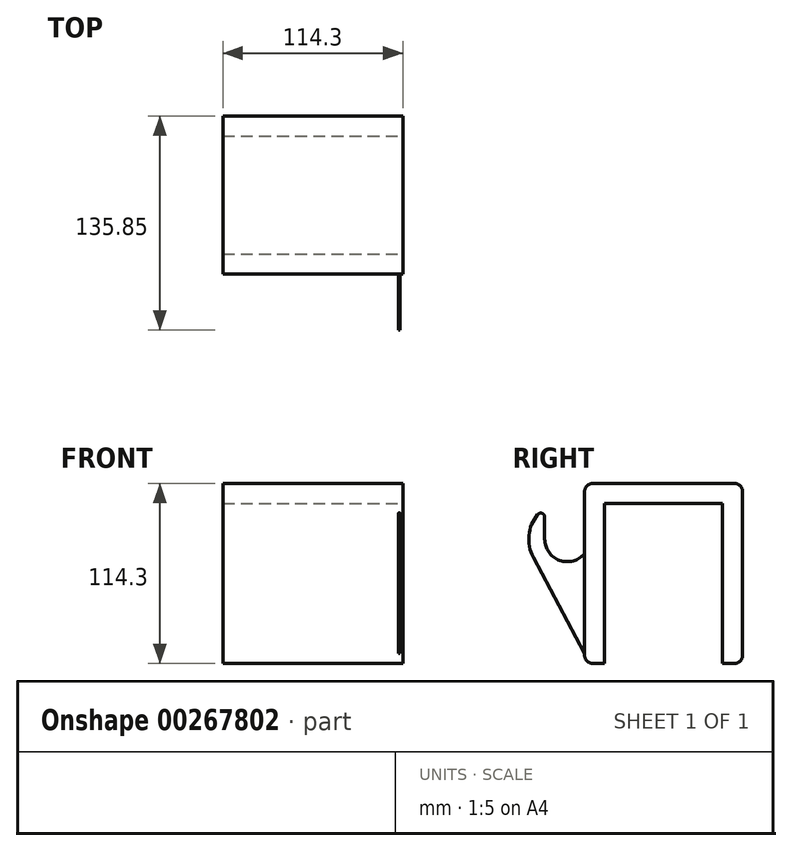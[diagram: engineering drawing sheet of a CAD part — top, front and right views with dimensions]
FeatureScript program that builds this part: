
annotation { "Feature Type Name" : "Feature", "Feature Type Description" : "" }
export const myFeature = defineFeature(function(context is Context, id is Id, definition is map)
    precondition{}
    {
        {
            var Q0;
            Q0=qCreatedBy(makeId("Top.planeOp"),FACE);
            var sketch = newSketch(context, id + "F0", { "sketchPlane" : qUnion([Q0])});
            skLineSegment(sketch, "E0.bottom", {"start": v(-114.3, 74.93) * mm, "end": v(0, 74.93) * mm});
            skLineSegment(sketch, "E0.top", {"start": v(-114.3, 0) * mm, "end": v(0, 0) * mm});
            skLineSegment(sketch, "E0.left", {"start": v(-114.3, 74.93) * mm, "end": v(-114.3, 0) * mm});
            skLineSegment(sketch, "E0.right", {"start": v(0, 74.93) * mm, "end": v(0, 0) * mm});
            skLineSegment(sketch, "E1", {"start": v(-114.3, 0) * mm, "end": v(-114.3, -12.7) * mm});
            skLineSegment(sketch, "E2", {"start": v(-114.3, -12.7) * mm, "end": v(0, -12.7) * mm});
            skLineSegment(sketch, "E3", {"start": v(0, -12.7) * mm, "end": v(0, 0) * mm});
            skLineSegment(sketch, "E4", {"start": v(-114.3, 74.93) * mm, "end": v(-114.3, 87.63) * mm});
            skLineSegment(sketch, "E5", {"start": v(-114.3, 87.63) * mm, "end": v(0, 87.63) * mm});
            skLineSegment(sketch, "E6", {"start": v(0, 87.63) * mm, "end": v(0, 74.93) * mm});
            skLineSegment(sketch, "E7", {"start": v(-101.6, 87.63) * mm, "end": v(-101.6, 74.93) * mm});
            skLineSegment(sketch, "E8", {"start": v(-12.7, 87.63) * mm, "end": v(-12.7, 74.93) * mm});
            skLineSegment(sketch, "E9", {"start": v(-12.7, 0) * mm, "end": v(-12.7, -12.7) * mm});
            skLineSegment(sketch, "E10", {"start": v(-101.6, 0) * mm, "end": v(-101.6, -12.7) * mm});
            skLineSegment(sketch, "E11", {"start": v(-101.6, 74.93) * mm, "end": v(-101.6, 0) * mm, "construction": true});
            skLineSegment(sketch, "E12", {"start": v(-12.7, 74.93) * mm, "end": v(-12.7, 0) * mm, "construction": true});
            skSolve(sketch);
        }
        {
            var Q0;
            {var subQ0=sQuery(id+"F0.wireOp",EDGE,"E0.left");Q0=makeQuery(id+"F0.imprint","IMPRINT",FACE,{"disambiguationData":[TD([[makeQuery(id+"F0.imprint","IMPRINT",EDGE,{"derivedFrom":subQ0}),1.0]])]});}
            extrude(context, id + "F1", {"entities" : qUnion([Q0]), "oppositeDirection" : true, "depth" : 12.7 * mm});
        }
        {
            var Q0;
            {var subQ0=sQuery(id+"F0.wireOp",EDGE,"E4");Q0=makeQuery(id+"F0.imprint","IMPRINT",FACE,{"disambiguationData":[TD([[makeQuery(id+"F0.imprint","IMPRINT",EDGE,{"derivedFrom":subQ0}),-1.0]])]});}
            var Q1;
            {var subQ0=sQuery(id+"F0.wireOp",EDGE,"E7");Q1=makeQuery(id+"F0.imprint","IMPRINT",FACE,{"disambiguationData":[TD([[makeQuery(id+"F0.imprint","IMPRINT",EDGE,{"derivedFrom":subQ0}),1.0]])]});}
            var Q2;
            {var subQ0=sQuery(id+"F0.wireOp",EDGE,"E6");Q2=makeQuery(id+"F0.imprint","IMPRINT",FACE,{"disambiguationData":[TD([[makeQuery(id+"F0.imprint","IMPRINT",EDGE,{"derivedFrom":subQ0}),-1.0]])]});}
            var Q3;
            {var subQ0=sQuery(id+"F0.wireOp",EDGE,"E3");Q3=makeQuery(id+"F0.imprint","IMPRINT",FACE,{"disambiguationData":[TD([[makeQuery(id+"F0.imprint","IMPRINT",EDGE,{"derivedFrom":subQ0}),1.0]])]});}
            var Q4;
            {var subQ0=sQuery(id+"F0.wireOp",EDGE,"E9");Q4=makeQuery(id+"F0.imprint","IMPRINT",FACE,{"disambiguationData":[TD([[makeQuery(id+"F0.imprint","IMPRINT",EDGE,{"derivedFrom":subQ0}),-1.0]])]});}
            var Q5;
            {var subQ0=sQuery(id+"F0.wireOp",EDGE,"E1");Q5=makeQuery(id+"F0.imprint","IMPRINT",FACE,{"disambiguationData":[TD([[makeQuery(id+"F0.imprint","IMPRINT",EDGE,{"derivedFrom":subQ0}),1.0]])]});}
            extrude(context, id + "F2", {"entities" : qUnion([Q0, Q1, Q2, Q3, Q4, Q5]), "operationType" : NewBodyOperationType.ADD, "oppositeDirection" : true, "depth" : 114.3 * mm});
        }
        {
            var Q0;
            Q0=qCreatedBy(makeId("Right.planeOp"),FACE);
            var sketch = newSketch(context, id + "F3", { "sketchPlane" : qUnion([Q0])});
            skLineSegment(sketch, "E13", {"start": v(0, 0) * mm, "end": v(-12.7, 0) * mm, "construction": true});
            skLineSegment(sketch, "E14", {"start": v(-12.7, 0) * mm, "end": v(-12.7, -44.45) * mm, "construction": true});
            skArc(sketch, "E15", {"start": v(-38.1, -35.35) * mm, "mid": v(-28.6, -48.84) * mm, "end": v(-12.7, -44.45) * mm});
            skLineSegment(sketch, "E16", {"start": v(-12.7, -44.45) * mm, "end": v(-12.7, -57.15) * mm});
            skArc(sketch, "E17", {"start": v(-38.1, -15.55) * mm, "mid": v(-44.64, -48.1) * mm, "end": v(-12.7, -57.15) * mm});
            skLineSegment(sketch, "E18", {"start": v(-38.1, -35.35) * mm, "end": v(-38.1, -15.55) * mm});
            skLineSegment(sketch, "E19", {"start": v(-12.7, -57.15) * mm, "end": v(-12.7, -107.95) * mm});
            skLineSegment(sketch, "E20", {"start": v(-12.7, -107.95) * mm, "end": v(-45.33, -46.87) * mm});
            skLineSegment(sketch, "E21", {"start": v(-38.1, -35.35) * mm, "end": v(-12.7, -35.35) * mm, "construction": true});
            skSolve(sketch);
        }
        {
            var Q0;
            Q0=makeQuery(id+"F2.opExtrude","CAP_EDGE",EDGE,{"disambiguationData":[OSD([sQuery(id+"F0.wireOp",EDGE,"E5")])],"isStart":true});
            var Q1;
            Q1=makeQuery(id+"F2.opExtrude","CAP_EDGE",EDGE,{"disambiguationData":[OSD([sQuery(id+"F0.wireOp",EDGE,"E5")])],"isStart":false});
            var Q2;
            Q2=makeQuery(id+"F2.opExtrude","CAP_EDGE",EDGE,{"disambiguationData":[OSD([sQuery(id+"F0.wireOp",EDGE,"E2")])],"isStart":true});
            fillet(context, id + "F4", {"entities" : qUnion([Q0, Q1, Q2]), "radius" : 5.08 * mm, "tangentPropagation" : true, "allowEdgeOverflow" : false});
        }
        {
            var Q0;
            Q0=makeQuery(id+"F3.imprint","IMPRINT",FACE,{"disambiguationData":[TD([[makeQuery(id+"F3.imprint","IMPRINT",EDGE,{"derivedFrom":sQuery(id+"F3.wireOp",EDGE,"E15")}),-1.0]])]});
            var Q1;
            {var subQ0=sQuery(id+"F3.wireOp",EDGE,"E19");Q1=makeQuery(id+"F3.imprint","IMPRINT",FACE,{"disambiguationData":[TD([[makeQuery(id+"F3.imprint","IMPRINT",EDGE,{"derivedFrom":subQ0}),-1.0]])]});}
            extrude(context, id + "F5", {"entities" : qUnion([Q0, Q1]), "oppositeDirection" : true, "depth" : ((4.5) / 2 + .5) * mm});
        }
        {
            var Q0;
            Q0=makeQuery(id+"F3.imprint","IMPRINT",FACE,{"disambiguationData":[TD([[makeQuery(id+"F3.imprint","IMPRINT",EDGE,{"derivedFrom":sQuery(id+"F3.wireOp",EDGE,"E15")}),-1.0]])]});
            var Q1;
            {var subQ0=sQuery(id+"F3.wireOp",EDGE,"E19");Q1=makeQuery(id+"F3.imprint","IMPRINT",FACE,{"disambiguationData":[TD([[makeQuery(id+"F3.imprint","IMPRINT",EDGE,{"derivedFrom":subQ0}),-1.0]])]});}
            extrude(context, id + "F6", {"entities" : qUnion([Q0, Q1]), "operationType" : NewBodyOperationType.REMOVE, "oppositeDirection" : true, "depth" : ((4.5) / 2 - .5) * mm});
        }
        {
            var Q0;
            Q0=makeQuery(id+"F5.opExtrude","SWEPT_EDGE",EDGE,{"disambiguationData":[OSD([sQuery(id+"F3.wireOp",EDGE,"E17"),sQuery(id+"F3.wireOp",EDGE,"E18")])]});
            fillet(context, id + "F7", {"entities" : qUnion([Q0]), "radius" : 2.54 * mm, "tangentPropagation" : true, "allowEdgeOverflow" : false});
        }
        {
            var Q0;
            Q0=makeQuery(id+"F2.opExtrude","CAP_EDGE",EDGE,{"disambiguationData":[OSD([sQuery(id+"F0.wireOp",EDGE,"E2")])],"isStart":true});
            var Q1;
            Q1=makeQuery(id+"F2.opExtrude","CAP_EDGE",EDGE,{"disambiguationData":[OSD([sQuery(id+"F0.wireOp",EDGE,"E2")])],"isStart":false});
            fillet(context, id + "F8", {"entities" : qUnion([Q0, Q1]), "radius" : 5.08 * mm, "tangentPropagation" : true, "allowEdgeOverflow" : false});
        }
    });
